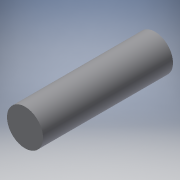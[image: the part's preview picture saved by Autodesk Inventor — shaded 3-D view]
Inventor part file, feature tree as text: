
AUTODESK INVENTOR PART (.ipt)
format: ipt  version: 2018 (Build 220112000, 112)  size: 91,648 bytes
history: native  units: mm
features: extrude x1, sketch x1
ambient origin geometry x8: Origin, YZ Plane, XZ Plane, XY Plane, X Axis, Y Axis, Z Axis, Center Point
bodies: Volumenkörper1 (feature_tree)
feature tree (2):
  extrude  "Extrusion1"  Depth=18.0mm TaperAngle=0.0deg
  sketch  "Skizze1"  dims[d0=5.0mm d1=18.0mm d2=0.0mm]
